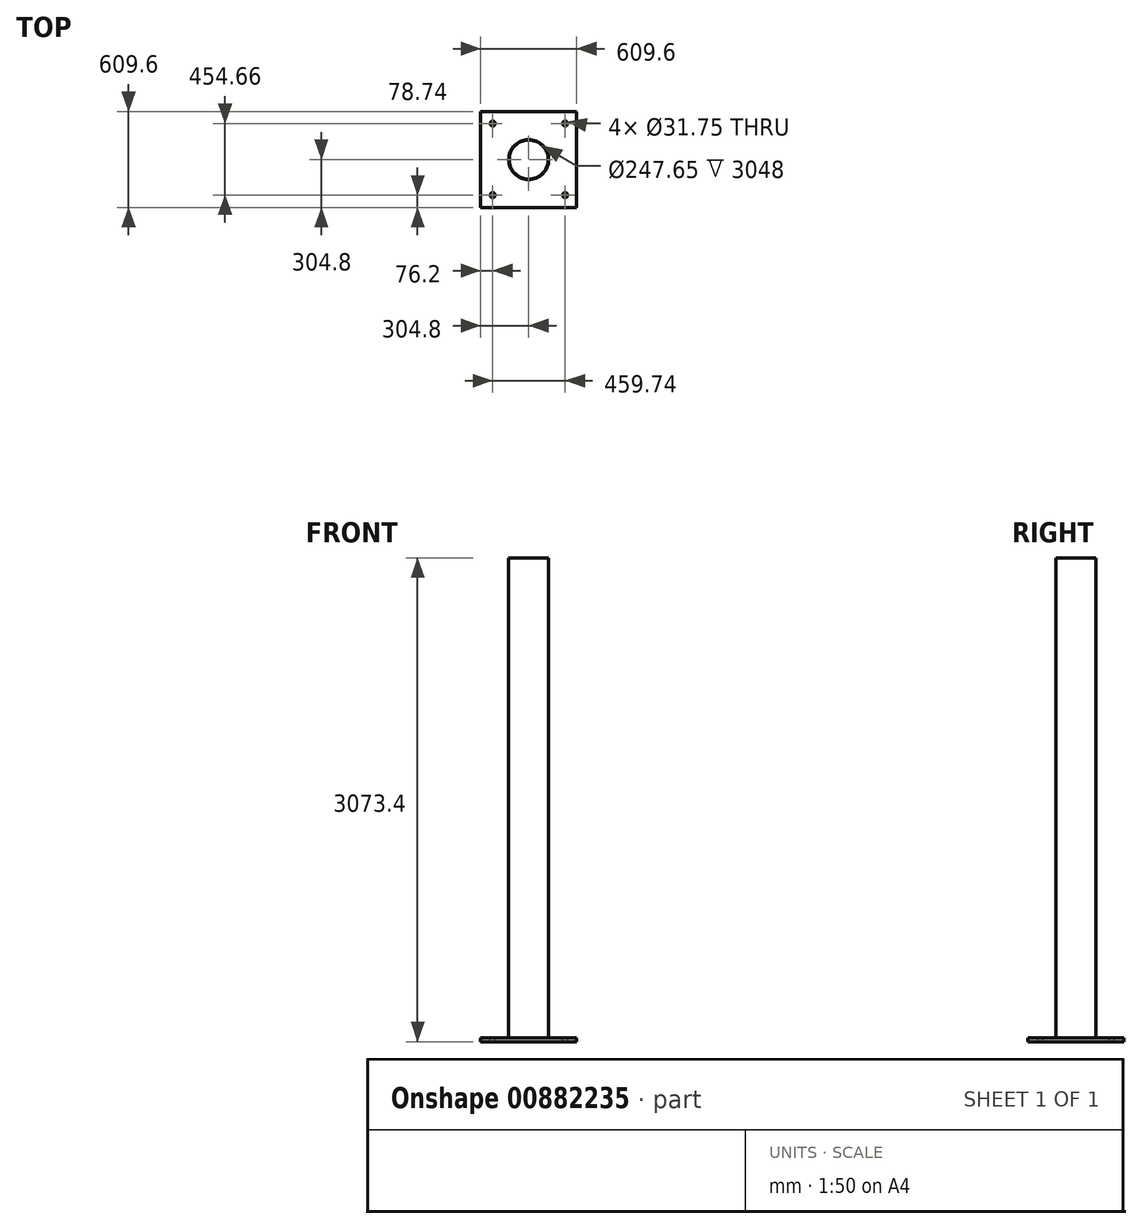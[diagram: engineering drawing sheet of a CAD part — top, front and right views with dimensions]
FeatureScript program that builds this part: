
annotation { "Feature Type Name" : "Feature", "Feature Type Description" : "" }
export const myFeature = defineFeature(function(context is Context, id is Id, definition is map)
    precondition{}
    {
        {
            var Q0;
            Q0=qCreatedBy(makeId("Front.planeOp"),FACE);
            var sketch = newSketch(context, id + "F0", { "sketchPlane" : qUnion([Q0])});
            skLineSegment(sketch, "E0.bottom", {"start": v(-304.8, 12.7) * mm, "end": v(304.8, 12.7) * mm});
            skLineSegment(sketch, "E0.top", {"start": v(-304.8, -12.7) * mm, "end": v(304.8, -12.7) * mm});
            skLineSegment(sketch, "E0.left", {"start": v(-304.8, 12.7) * mm, "end": v(-304.8, -12.7) * mm});
            skLineSegment(sketch, "E0.right", {"start": v(304.8, 12.7) * mm, "end": v(304.8, -12.7) * mm});
            skSolve(sketch);
        }
        {
            var Q0;
            Q0=makeQuery(id+"F0.imprint","IMPRINT",FACE,{"disambiguationData":[TD([[makeQuery(id+"F0.imprint","IMPRINT",EDGE,{"derivedFrom":sQuery(id+"F0.wireOp",EDGE,"E0.bottom")}),-1.0]])]});
            extrude(context, id + "F1", {"entities" : qUnion([Q0]), "depth" : 304.8 * mm, "offsetDistance" : 25.4 * mm});
        }
        {
            var Q0;
            Q0=makeQuery(id+"F1.opExtrude","CAP_FACE",FACE,{"disambiguationData":[OSD([sQuery(id+"F0.wireOp",EDGE,"E0.bottom"),sQuery(id+"F0.wireOp",EDGE,"E0.top"),sQuery(id+"F0.wireOp",EDGE,"E0.left"),sQuery(id+"F0.wireOp",EDGE,"E0.right")])],"isStart":true});
            extrude(context, id + "F2", {"entities" : qUnion([Q0]), "operationType" : NewBodyOperationType.ADD, "depth" : 304.8 * mm, "offsetDistance" : 25.4 * mm});
        }
        {
            var Q0;
            {var subQ0=sQuery(id+"F0.wireOp",EDGE,"E0.bottom");Q0=makeQuery(id+"F2.boolean.opBoolean","MERGE",FACE,{"derivedFrom":[makeQuery(id+"F1.opExtrude","SWEPT_FACE",FACE,{"disambiguationData":[OSD([subQ0])]}),makeQuery(id+"F2.opExtrude","SWEPT_FACE",FACE,{"disambiguationData":[OSD([subQ0])]})]});}
            var sketch = newSketch(context, id + "F3", { "sketchPlane" : qUnion([Q0])});
            skCircle(sketch, "E1", {"center": v(0, 0) * mm, "radius": 127 * mm});
            skCircle(sketch, "E2", {"center": v(0, 0) * mm, "radius": 123.83 * mm});
            skSolve(sketch);
        }
        {
            var Q0;
            Q0=makeQuery(id+"F3.imprint","IMPRINT",FACE,{"disambiguationData":[TD([[makeQuery(id+"F3.imprint","IMPRINT",EDGE,{"derivedFrom":sQuery(id+"F3.wireOp",EDGE,"E1")}),1.0]])]});
            extrude(context, id + "F4", {"entities" : qUnion([Q0]), "operationType" : NewBodyOperationType.ADD, "depth" : 3048 * mm, "offsetDistance" : 25.4 * mm});
        }
        {
            var Q0;
            {var subQ0=sQuery(id+"F0.wireOp",EDGE,"E0.left");var subQ3=sQuery(id+"F0.wireOp",EDGE,"E0.bottom");Q0=makeQuery(id+"F4.boolean.opBoolean","SPLIT",FACE,{"disambiguationData":[TD([makeQuery(id+"F1.opExtrude","SWEPT_FACE",FACE,{"disambiguationData":[OSD([subQ0])]})])],"derivedFrom":makeQuery(id+"F2.boolean.opBoolean","MERGE",FACE,{"derivedFrom":[makeQuery(id+"F1.opExtrude","SWEPT_FACE",FACE,{"disambiguationData":[OSD([subQ3])]}),makeQuery(id+"F2.opExtrude","SWEPT_FACE",FACE,{"disambiguationData":[OSD([subQ3])]})]})});}
            var sketch = newSketch(context, id + "F5", { "sketchPlane" : qUnion([Q0])});
            skCircle(sketch, "E3", {"center": v(-228.6, 228.6) * mm, "radius": 15.88 * mm});
            skCircle(sketch, "E4.0.1.0", {"center": v(-228.6, -226.06) * mm, "radius": 15.88 * mm});
            skCircle(sketch, "E4.1.0.0", {"center": v(231.14, 228.6) * mm, "radius": 15.88 * mm});
            skCircle(sketch, "E4.1.1.0", {"center": v(231.14, -226.06) * mm, "radius": 15.88 * mm});
            skLineSegment(sketch, "E4.direction1", {"start": v(-228.6, 228.6) * mm, "end": v(231.14, 228.6) * mm, "construction": true});
            skLineSegment(sketch, "E4.direction2", {"start": v(-228.6, 228.6) * mm, "end": v(-228.6, -226.06) * mm, "construction": true});
            skSolve(sketch);
        }
        {
            var Q0;
            Q0=sQuery(id+"F5.wireOp",VERTEX,"E4.direction1.start");
            var Q1;
            Q1=sQuery(id+"F5.wireOp",VERTEX,"E4.direction2.end");
            var Q2;
            Q2=sQuery(id+"F5.wireOp",VERTEX,"E4.1.1.0.center");
            var Q3;
            Q3=sQuery(id+"F5.wireOp",VERTEX,"E4.direction1.end");
            var Q4;
            Q4=makeQuery(id+"F1.opExtrude","SWEPT_BODY",BODY,{"disambiguationData":[OSD([sQuery(id+"F0.wireOp",EDGE,"E0.bottom"),sQuery(id+"F0.wireOp",EDGE,"E0.top"),sQuery(id+"F0.wireOp",EDGE,"E0.left"),sQuery(id+"F0.wireOp",EDGE,"E0.right")])]});
            hole(context, id + "F6", {"style" : HoleStyle.SIMPLE, "endStyle" : HoleEndStyle.THROUGH, "holeDiameter" : 31.75 * mm, "majorDiameter" : 6.35 * mm, "isTappedThrough" : true, "tappedDepth" : 12.7 * mm, "tapClearance" : 3, "locations" : qUnion([Q0, Q1, Q2, Q3]), "scope" : qUnion([Q4])});
        }
    });
